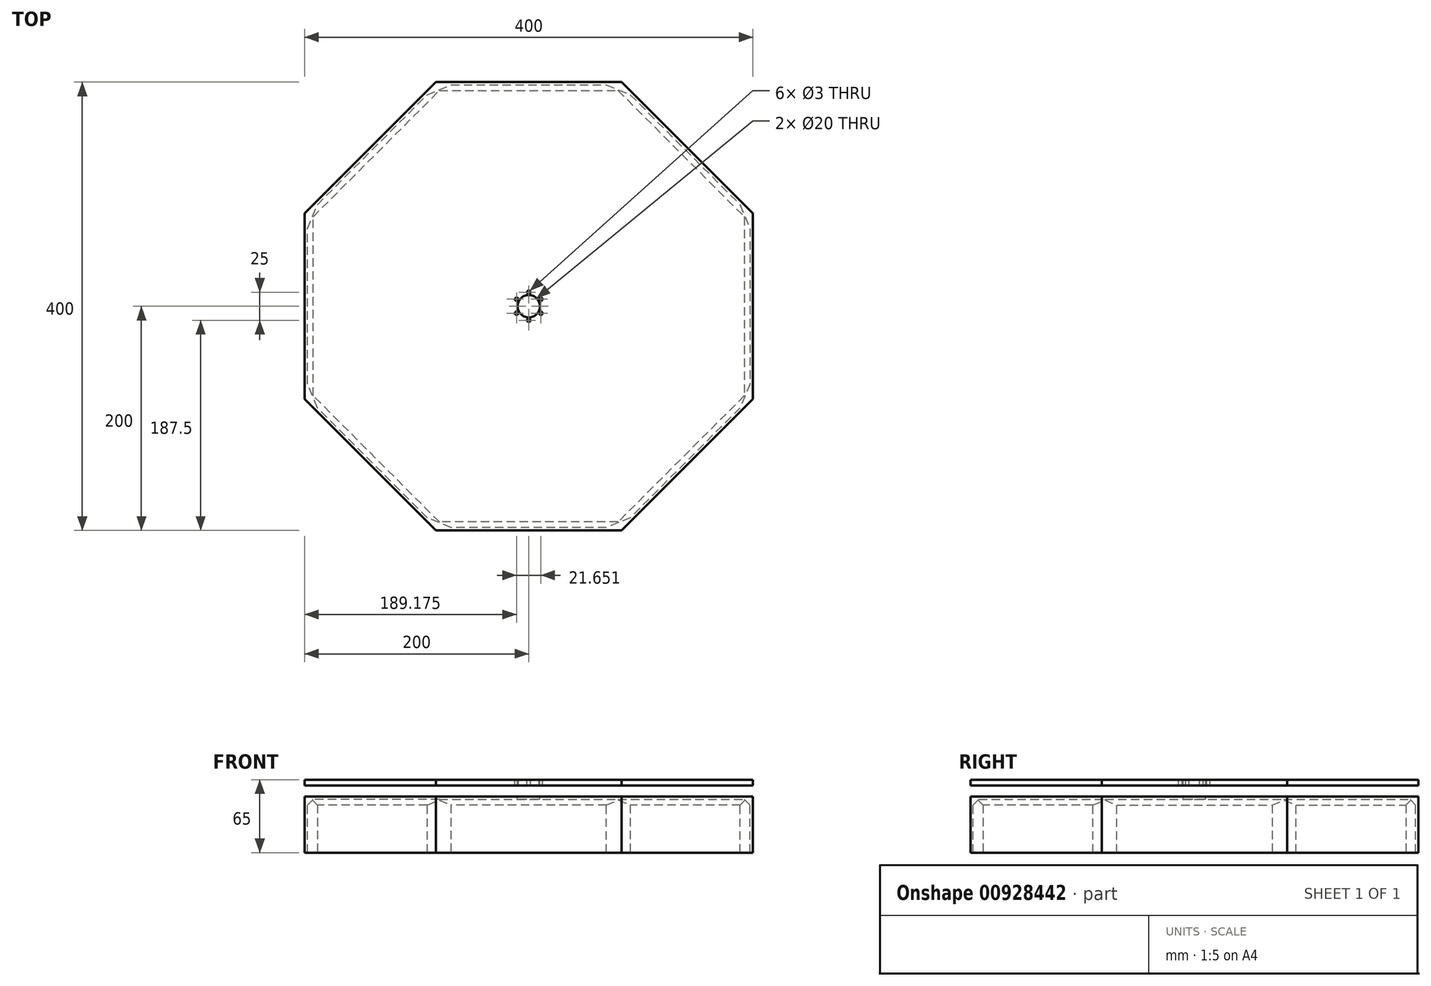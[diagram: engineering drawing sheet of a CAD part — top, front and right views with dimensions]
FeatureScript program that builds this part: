
annotation { "Feature Type Name" : "Feature", "Feature Type Description" : "" }
export const myFeature = defineFeature(function(context is Context, id is Id, definition is map)
    precondition{}
    {
        {
            var Q0;
            Q0=qCreatedBy(makeId("Top.planeOp"),FACE);
            var sketch = newSketch(context, id + "F0", { "sketchPlane" : qUnion([Q0])});
            skCircle(sketch, "E0.cCircle", {"center": v(0, 0) * mm, "radius": 200 * mm, "construction": true});
            skLineSegment(sketch, "E0.0", {"start": v(200, 82.84) * mm, "end": v(200, -82.84) * mm});
            skLineSegment(sketch, "E0.1", {"start": v(200, -82.84) * mm, "end": v(82.84, -200) * mm});
            skLineSegment(sketch, "E0.2", {"start": v(82.84, -200) * mm, "end": v(-82.84, -200) * mm});
            skLineSegment(sketch, "E0.3", {"start": v(-82.84, -200) * mm, "end": v(-200, -82.84) * mm});
            skLineSegment(sketch, "E0.4", {"start": v(-200, -82.84) * mm, "end": v(-200, 82.84) * mm});
            skLineSegment(sketch, "E0.5", {"start": v(-200, 82.84) * mm, "end": v(-82.84, 200) * mm});
            skLineSegment(sketch, "E0.6", {"start": v(-82.84, 200) * mm, "end": v(82.84, 200) * mm});
            skLineSegment(sketch, "E0.7", {"start": v(82.84, 200) * mm, "end": v(200, 82.84) * mm});
            skPoint(sketch, "E0.0.midPoint", {"position": v(200, 0) * mm});
            skSolve(sketch);
        }
        {
            var Q0;
            Q0=makeQuery(id+"F0.imprint","IMPRINT",FACE,{"disambiguationData":[TD([[makeQuery(id+"F0.imprint","IMPRINT",EDGE,{"derivedFrom":sQuery(id+"F0.wireOp",EDGE,"E0.0")}),-1.0]])]});
            extrude(context, id + "F1", {"entities" : qUnion([Q0]), "oppositeDirection" : true, "depth" : 50 * mm, "offsetDistance" : 25 * mm});
        }
        {
            var Q0;
            Q0=makeQuery(id+"F1.opExtrude","CAP_FACE",FACE,{"disambiguationData":[OSD([sQuery(id+"F0.wireOp",EDGE,"E0.0"),sQuery(id+"F0.wireOp",EDGE,"E0.1"),sQuery(id+"F0.wireOp",EDGE,"E0.2"),sQuery(id+"F0.wireOp",EDGE,"E0.3"),sQuery(id+"F0.wireOp",EDGE,"E0.4"),sQuery(id+"F0.wireOp",EDGE,"E0.5"),sQuery(id+"F0.wireOp",EDGE,"E0.6"),sQuery(id+"F0.wireOp",EDGE,"E0.7")])],"isStart":true});
            var sketch = newSketch(context, id + "F2", { "sketchPlane" : qUnion([Q0])});
            skLineSegment(sketch, "E1.0", {"start": v(-82.84, 200) * mm, "end": v(82.84, 200) * mm});
            skLineSegment(sketch, "E2.0", {"start": v(82.84, 200) * mm, "end": v(200, 82.84) * mm});
            skLineSegment(sketch, "E3.0", {"start": v(200, 82.84) * mm, "end": v(200, -82.84) * mm});
            skLineSegment(sketch, "E4.1", {"start": v(200, -82.84) * mm, "end": v(82.84, -200) * mm});
            skLineSegment(sketch, "E5.0", {"start": v(82.84, -200) * mm, "end": v(-82.84, -200) * mm});
            skLineSegment(sketch, "E6.0", {"start": v(-82.84, -200) * mm, "end": v(-200, -82.84) * mm});
            skLineSegment(sketch, "E7.1", {"start": v(-200, -82.84) * mm, "end": v(-200, 82.84) * mm});
            skLineSegment(sketch, "E8.0", {"start": v(-200, 82.84) * mm, "end": v(-82.84, 200) * mm});
            skSolve(sketch);
        }
        {
            var Q0;
            Q0 = qSketchRegion(id + "F2", true);
            extrude(context, id + "F3", {"entities" : qUnion([Q0]), "depth" : 15 * mm, "offsetDistance" : 25 * mm, "hasSecondDirection" : true, "secondDirectionOppositeDirection" : true, "secondDirectionDepth" : -10 * mm});
        }
        {
            var Q0;
            Q0=makeQuery(id+"F1.opExtrude","CAP_FACE",FACE,{"disambiguationData":[OSD([sQuery(id+"F0.wireOp",EDGE,"E0.0"),sQuery(id+"F0.wireOp",EDGE,"E0.1"),sQuery(id+"F0.wireOp",EDGE,"E0.2"),sQuery(id+"F0.wireOp",EDGE,"E0.3"),sQuery(id+"F0.wireOp",EDGE,"E0.4"),sQuery(id+"F0.wireOp",EDGE,"E0.5"),sQuery(id+"F0.wireOp",EDGE,"E0.6"),sQuery(id+"F0.wireOp",EDGE,"E0.7")])],"isStart":false});
            shell(context, id + "F4", {"entities" : qUnion([Q0]), "thickness" : 2.5 * mm});
        }
        {
            var Q0;
            Q0=makeQuery(id+"F3.opExtrude","CAP_FACE",FACE,{"disambiguationData":[OSD([sQuery(id+"F2.wireOp",EDGE,"E1.0"),sQuery(id+"F2.wireOp",EDGE,"E2.0"),sQuery(id+"F2.wireOp",EDGE,"E3.0"),sQuery(id+"F2.wireOp",EDGE,"E4.1"),sQuery(id+"F2.wireOp",EDGE,"E5.0"),sQuery(id+"F2.wireOp",EDGE,"E6.0"),sQuery(id+"F2.wireOp",EDGE,"E7.1"),sQuery(id+"F2.wireOp",EDGE,"E8.0")])],"isStart":false});
            var sketch = newSketch(context, id + "F5", { "sketchPlane" : qUnion([Q0])});
            skCircle(sketch, "E9", {"center": v(0, 0) * mm, "radius": 10 * mm});
            skSolve(sketch);
        }
        {
            var Q0;
            Q0=makeQuery(id+"F5.imprint","IMPRINT",FACE,{"disambiguationData":[TD([[makeQuery(id+"F5.imprint","IMPRINT",EDGE,{"derivedFrom":sQuery(id+"F5.wireOp",EDGE,"E9")}),1.0]])]});
            extrude(context, id + "F6", {"entities" : qUnion([Q0]), "operationType" : NewBodyOperationType.REMOVE, "endBound" : BoundingType.THROUGH_ALL, "oppositeDirection" : true, "depth" : 25 * mm, "offsetDistance" : 25 * mm});
        }
        {
            var Q0;
            Q0=makeQuery(id+"F3.opExtrude","CAP_FACE",FACE,{"disambiguationData":[OSD([sQuery(id+"F2.wireOp",EDGE,"E1.0"),sQuery(id+"F2.wireOp",EDGE,"E2.0"),sQuery(id+"F2.wireOp",EDGE,"E3.0"),sQuery(id+"F2.wireOp",EDGE,"E4.1"),sQuery(id+"F2.wireOp",EDGE,"E5.0"),sQuery(id+"F2.wireOp",EDGE,"E6.0"),sQuery(id+"F2.wireOp",EDGE,"E7.1"),sQuery(id+"F2.wireOp",EDGE,"E8.0")])],"isStart":false});
            var sketch = newSketch(context, id + "F7", { "sketchPlane" : qUnion([Q0])});
            skCircle(sketch, "E10", {"center": v(0, 0) * mm, "radius": 12.5 * mm, "construction": true});
            skLineSegment(sketch, "E11", {"start": v(0, 0) * mm, "end": v(0, 12.5) * mm, "construction": true});
            skCircle(sketch, "E12", {"center": v(0, 12.5) * mm, "radius": 1.5 * mm});
            skCircle(sketch, "E13.1.0", {"center": v(-10.83, 6.25) * mm, "radius": 1.5 * mm});
            skCircle(sketch, "E13.2.0", {"center": v(-10.83, -6.25) * mm, "radius": 1.5 * mm});
            skCircle(sketch, "E13.3.0", {"center": v(0, -12.5) * mm, "radius": 1.5 * mm});
            skCircle(sketch, "E13.4.0", {"center": v(10.83, -6.25) * mm, "radius": 1.5 * mm});
            skCircle(sketch, "E13.5.0", {"center": v(10.83, 6.25) * mm, "radius": 1.5 * mm});
            skLineSegment(sketch, "E13.anchor2", {"start": v(0, 0) * mm, "end": v(10.83, 6.25) * mm, "construction": true});
            skSolve(sketch);
        }
        {
            var Q0;
            Q0 = qSketchRegion(id + "F7", true);
            extrude(context, id + "F8", {"entities" : qUnion([Q0]), "operationType" : NewBodyOperationType.REMOVE, "oppositeDirection" : true, "depth" : 15 * mm, "offsetDistance" : 25 * mm});
        }
        {
            var Q0;
            Q0=makeQuery(id+"F4.opShell","OFFSET_EDGE",EDGE,{"disambiguationData":[OSD([sQuery(id+"F0.wireOp",EDGE,"E0.2"),sQuery(id+"F0.wireOp",EDGE,"E0.3")])]});
            var Q1;
            Q1=makeQuery(id+"F4.opShell","OFFSET_EDGE",EDGE,{"disambiguationData":[OSD([sQuery(id+"F0.wireOp",EDGE,"E0.1"),sQuery(id+"F0.wireOp",EDGE,"E0.2")])]});
            var Q2;
            Q2=makeQuery(id+"F4.opShell","OFFSET_EDGE",EDGE,{"disambiguationData":[OSD([sQuery(id+"F0.wireOp",EDGE,"E0.0"),sQuery(id+"F0.wireOp",EDGE,"E0.1")])]});
            var Q3;
            Q3=makeQuery(id+"F4.opShell","OFFSET_EDGE",EDGE,{"disambiguationData":[OSD([sQuery(id+"F0.wireOp",EDGE,"E0.0"),sQuery(id+"F0.wireOp",EDGE,"E0.7")])]});
            var Q4;
            Q4=makeQuery(id+"F4.opShell","OFFSET_EDGE",EDGE,{"disambiguationData":[OSD([sQuery(id+"F0.wireOp",EDGE,"E0.6"),sQuery(id+"F0.wireOp",EDGE,"E0.7")])]});
            var Q5;
            Q5=makeQuery(id+"F4.opShell","OFFSET_EDGE",EDGE,{"disambiguationData":[OSD([sQuery(id+"F0.wireOp",EDGE,"E0.5"),sQuery(id+"F0.wireOp",EDGE,"E0.6")])]});
            var Q6;
            Q6=makeQuery(id+"F4.opShell","OFFSET_EDGE",EDGE,{"disambiguationData":[OSD([sQuery(id+"F0.wireOp",EDGE,"E0.4"),sQuery(id+"F0.wireOp",EDGE,"E0.5")])]});
            var Q7;
            Q7=makeQuery(id+"F4.opShell","OFFSET_EDGE",EDGE,{"disambiguationData":[OSD([sQuery(id+"F0.wireOp",EDGE,"E0.3"),sQuery(id+"F0.wireOp",EDGE,"E0.4")])]});
            chamfer(context, id + "F9", {"entities" : qUnion([Q0, Q1, Q2, Q3, Q4, Q5, Q6, Q7]), "width" : 30 * mm, "tangentPropagation" : true});
        }
        {
            var Q0;
            {var subQ0=sQuery(id+"F0.wireOp",EDGE,"E0.3");Q0=makeQuery(id+"F4.opShell","OFFSET_EDGE",EDGE,{"disambiguationData":[OSD([subQ0]),TDD([makeQuery(id+"F1.opExtrude","CAP_EDGE",EDGE,{"disambiguationData":[OSD([subQ0])],"isStart":true})])]});}
            var Q1;
            {var subQ0=sQuery(id+"F0.wireOp",EDGE,"E0.2");Q1=makeQuery(id+"F4.opShell","OFFSET_EDGE",EDGE,{"disambiguationData":[OSD([subQ0]),TDD([makeQuery(id+"F1.opExtrude","CAP_EDGE",EDGE,{"disambiguationData":[OSD([subQ0])],"isStart":true})])]});}
            var Q2;
            {var subQ0=sQuery(id+"F0.wireOp",EDGE,"E0.1");Q2=makeQuery(id+"F4.opShell","OFFSET_EDGE",EDGE,{"disambiguationData":[OSD([subQ0]),TDD([makeQuery(id+"F1.opExtrude","CAP_EDGE",EDGE,{"disambiguationData":[OSD([subQ0])],"isStart":true})])]});}
            var Q3;
            {var subQ0=sQuery(id+"F0.wireOp",EDGE,"E0.0");Q3=makeQuery(id+"F4.opShell","OFFSET_EDGE",EDGE,{"disambiguationData":[OSD([subQ0]),TDD([makeQuery(id+"F1.opExtrude","CAP_EDGE",EDGE,{"disambiguationData":[OSD([subQ0])],"isStart":true})])]});}
            var Q4;
            {var subQ0=sQuery(id+"F0.wireOp",EDGE,"E0.7");Q4=makeQuery(id+"F4.opShell","OFFSET_EDGE",EDGE,{"disambiguationData":[OSD([subQ0]),TDD([makeQuery(id+"F1.opExtrude","CAP_EDGE",EDGE,{"disambiguationData":[OSD([subQ0])],"isStart":true})])]});}
            var Q5;
            {var subQ0=sQuery(id+"F0.wireOp",EDGE,"E0.6");Q5=makeQuery(id+"F4.opShell","OFFSET_EDGE",EDGE,{"disambiguationData":[OSD([subQ0]),TDD([makeQuery(id+"F1.opExtrude","CAP_EDGE",EDGE,{"disambiguationData":[OSD([subQ0])],"isStart":true})])]});}
            var Q6;
            {var subQ0=sQuery(id+"F0.wireOp",EDGE,"E0.5");Q6=makeQuery(id+"F4.opShell","OFFSET_EDGE",EDGE,{"disambiguationData":[OSD([subQ0]),TDD([makeQuery(id+"F1.opExtrude","CAP_EDGE",EDGE,{"disambiguationData":[OSD([subQ0])],"isStart":true})])]});}
            var Q7;
            {var subQ0=sQuery(id+"F0.wireOp",EDGE,"E0.4");Q7=makeQuery(id+"F4.opShell","OFFSET_EDGE",EDGE,{"disambiguationData":[OSD([subQ0]),TDD([makeQuery(id+"F1.opExtrude","CAP_EDGE",EDGE,{"disambiguationData":[OSD([subQ0])],"isStart":true})])]});}
            chamfer(context, id + "F10", {"entities" : qUnion([Q0, Q1, Q2, Q3, Q4, Q5, Q6, Q7]), "width" : 5 * mm, "tangentPropagation" : true});
        }
    });
